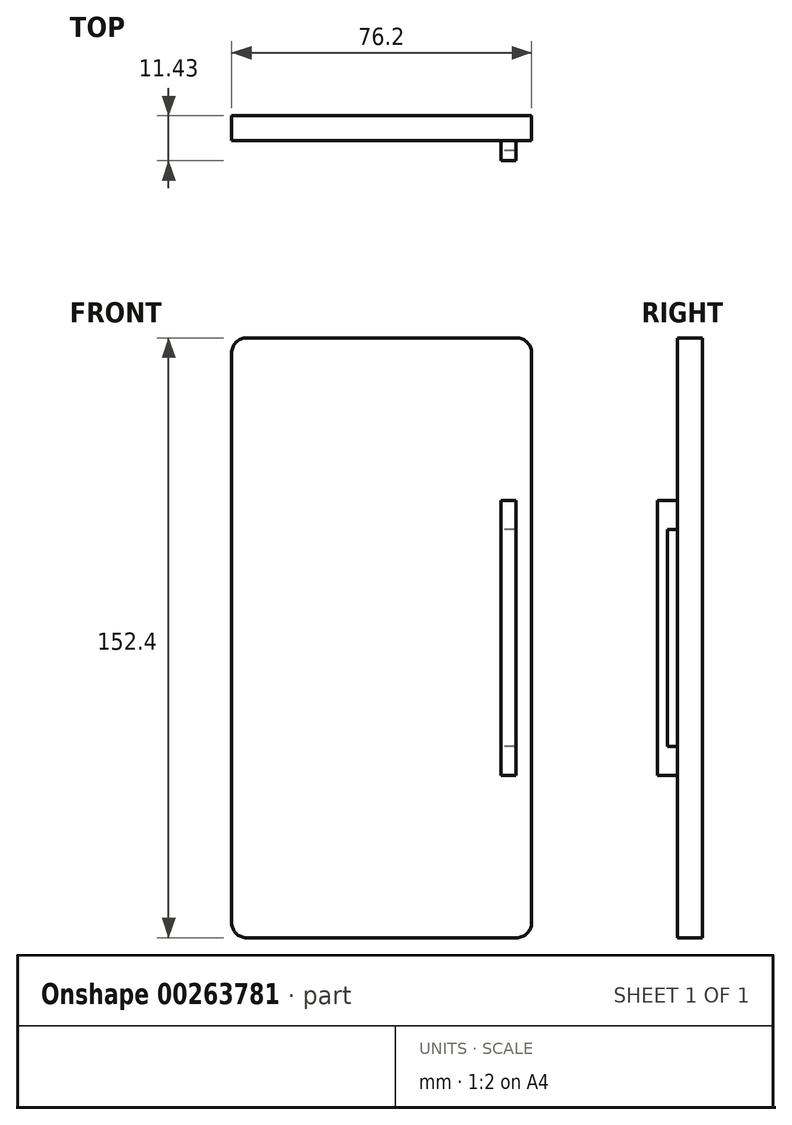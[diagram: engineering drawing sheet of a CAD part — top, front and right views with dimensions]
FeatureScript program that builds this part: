
annotation { "Feature Type Name" : "Feature", "Feature Type Description" : "" }
export const myFeature = defineFeature(function(context is Context, id is Id, definition is map)
    precondition{}
    {
        {
            var Q0;
            Q0=qCreatedBy(makeId("Front.planeOp"),FACE);
            var sketch = newSketch(context, id + "F0", { "sketchPlane" : qUnion([Q0])});
            skLineSegment(sketch, "E0.bottom", {"start": v(34.3, 76.2) * mm, "end": v(-34.29, 76.2) * mm});
            skLineSegment(sketch, "E0.top", {"start": v(34.29, -76.2) * mm, "end": v(-34.29, -76.2) * mm});
            skLineSegment(sketch, "E0.left", {"start": v(38.1, 72.4) * mm, "end": v(38.1, -72.39) * mm});
            skLineSegment(sketch, "E0.right", {"start": v(-38.1, 72.4) * mm, "end": v(-38.1, -72.39) * mm});
            skPoint(sketch, "E0.middle", {"position": v(0, 0) * mm});
            skPoint(sketch, "E1.visualSharp", {"position": v(-38.1, 76.2) * mm});
            skArc(sketch, "E1.filletArc", {"start": v(-34.29, 76.2) * mm, "mid": v(-36.98, 75.08) * mm, "end": v(-38.1, 72.4) * mm});
            skPoint(sketch, "E2.visualSharp", {"position": v(38.1, 76.2) * mm});
            skArc(sketch, "E2.filletArc", {"start": v(38.1, 72.4) * mm, "mid": v(36.98, 75.08) * mm, "end": v(34.3, 76.2) * mm});
            skPoint(sketch, "E3.visualSharp", {"position": v(38.1, -76.2) * mm});
            skArc(sketch, "E3.filletArc", {"start": v(34.29, -76.2) * mm, "mid": v(36.98, -75.08) * mm, "end": v(38.1, -72.39) * mm});
            skPoint(sketch, "E4.visualSharp", {"position": v(-38.1, -76.2) * mm});
            skArc(sketch, "E4.filletArc", {"start": v(-38.1, -72.39) * mm, "mid": v(-36.98, -75.08) * mm, "end": v(-34.29, -76.2) * mm});
            skSolve(sketch);
        }
        {
            var Q0;
            Q0=makeQuery(id+"F0.imprint","IMPRINT",FACE,{"disambiguationData":[TD([[makeQuery(id+"F0.imprint","IMPRINT",EDGE,{"derivedFrom":sQuery(id+"F0.wireOp",EDGE,"E0.bottom")}),1.0]])]});
            extrude(context, id + "F1", {"entities" : qUnion([Q0]), "depth" : 6.35 * mm});
        }
        {
            var Q0;
            Q0=makeQuery(id+"F1.opExtrude","CAP_FACE",FACE,{"disambiguationData":[OSD([sQuery(id+"F0.wireOp",EDGE,"E0.bottom"),sQuery(id+"F0.wireOp",EDGE,"E0.top"),sQuery(id+"F0.wireOp",EDGE,"E0.left"),sQuery(id+"F0.wireOp",EDGE,"E0.right"),sQuery(id+"F0.wireOp",EDGE,"E1.filletArc"),sQuery(id+"F0.wireOp",EDGE,"E2.filletArc"),sQuery(id+"F0.wireOp",EDGE,"E3.filletArc"),sQuery(id+"F0.wireOp",EDGE,"E4.filletArc")])],"isStart":false});
            var sketch = newSketch(context, id + "F2", { "sketchPlane" : qUnion([Q0])});
            skLineSegment(sketch, "E5.bottom", {"start": v(34.17, 34.93) * mm, "end": v(30.36, 34.93) * mm});
            skLineSegment(sketch, "E5.top", {"start": v(34.17, -34.93) * mm, "end": v(30.36, -34.93) * mm});
            skLineSegment(sketch, "E5.left", {"start": v(34.17, 34.93) * mm, "end": v(34.17, -34.93) * mm});
            skLineSegment(sketch, "E5.right", {"start": v(30.36, 34.93) * mm, "end": v(30.36, -34.93) * mm});
            skPoint(sketch, "E5.middle", {"position": v(32.26, 0) * mm});
            skSolve(sketch);
        }
        {
            var Q0;
            Q0=makeQuery(id+"F2.imprint","IMPRINT",FACE,{"disambiguationData":[TD([[makeQuery(id+"F2.imprint","IMPRINT",EDGE,{"derivedFrom":sQuery(id+"F2.wireOp",EDGE,"E5.bottom")}),1.0]])]});
            extrude(context, id + "F3", {"entities" : qUnion([Q0]), "operationType" : NewBodyOperationType.ADD, "depth" : 5.08 * mm});
        }
        {
            var Q0;
            Q0=makeQuery(id+"F3.opExtrude","SWEPT_FACE",FACE,{"disambiguationData":[OSD([sQuery(id+"F2.wireOp",EDGE,"E5.right")])]});
            var sketch = newSketch(context, id + "F4", { "sketchPlane" : qUnion([Q0])});
            skLineSegment(sketch, "E6", {"start": v(6.35, 0) * mm, "end": v(6.35, 27.56) * mm});
            skLineSegment(sketch, "E7", {"start": v(6.35, 0) * mm, "end": v(6.35, -27.56) * mm});
            skLineSegment(sketch, "E8", {"start": v(6.35, -27.56) * mm, "end": v(8.9, -27.56) * mm});
            skLineSegment(sketch, "E9", {"start": v(8.9, -27.56) * mm, "end": v(8.9, 27.56) * mm});
            skLineSegment(sketch, "E10", {"start": v(8.9, 27.56) * mm, "end": v(6.35, 27.56) * mm});
            skSolve(sketch);
        }
        {
            var Q0;
            Q0 = qSketchRegion(id + "F4", true);
            extrude(context, id + "F5", {"entities" : qUnion([Q0]), "operationType" : NewBodyOperationType.REMOVE, "oppositeDirection" : true, "depth" : 25.4 * mm});
        }
    });
